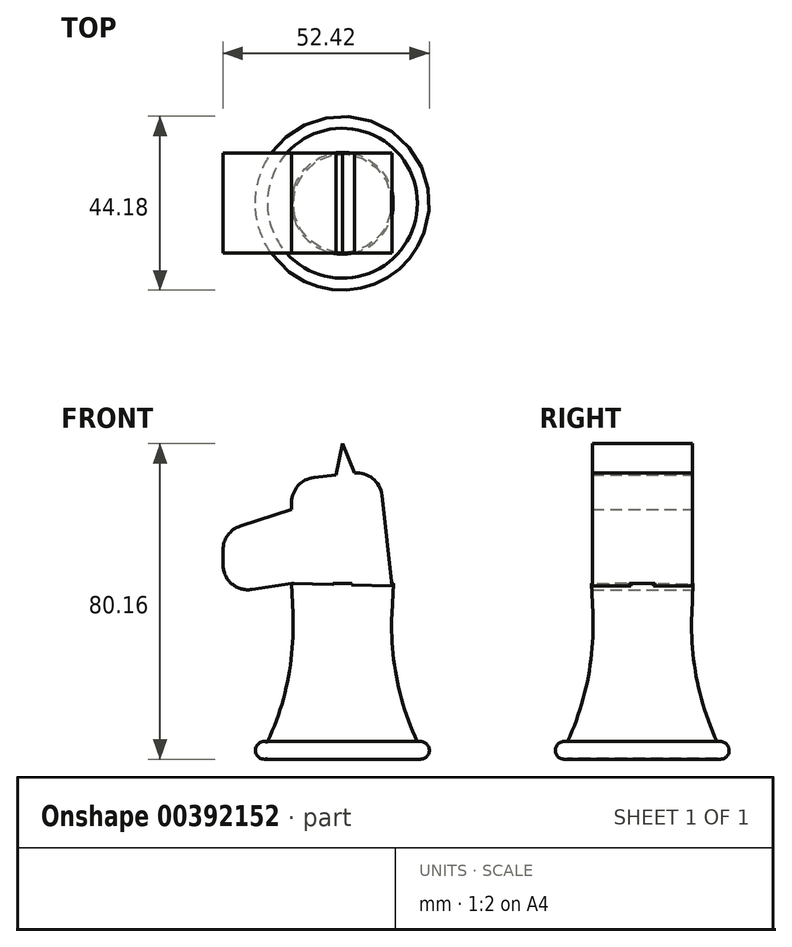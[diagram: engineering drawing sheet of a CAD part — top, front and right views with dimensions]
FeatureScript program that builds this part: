
annotation { "Feature Type Name" : "Feature", "Feature Type Description" : "" }
export const myFeature = defineFeature(function(context is Context, id is Id, definition is map)
    precondition{}
    {
        {
            var Q0;
            Q0=qCreatedBy(makeId("Front.planeOp"),FACE);
            var sketch = newSketch(context, id + "F0", { "sketchPlane" : qUnion([Q0])});
            skLineSegment(sketch, "E0", {"start": v(0, -50.97) * mm, "end": v(0, 6.18) * mm});
            skLineSegment(sketch, "E1", {"start": v(0, -50.97) * mm, "end": v(-19.05, -50.97) * mm});
            skArc(sketch, "E2", {"start": v(-19.05, -46.78) * mm, "mid": v(-22.09, -48.88) * mm, "end": v(-19.05, -50.97) * mm});
            skArc(sketch, "E3", {"start": v(-19.05, -46.78) * mm, "mid": v(-13.85, -30.88) * mm, "end": v(-12.58, -14.2) * mm});
            skLineSegment(sketch, "E4", {"start": v(-12.58, -14.2) * mm, "end": v(-12.92, -6.47) * mm});
            skLineSegment(sketch, "E5", {"start": v(-12.92, -6.47) * mm, "end": v(0, -6.47) * mm});
            skSolve(sketch);
        }
        {
            var Q0;
            Q0 = qSketchRegion(id + "F0", true);
            var Q1;
            Q1=sQuery(id+"F0.wireOp",EDGE,"E0");
            revolve(context, id + "F1", {"entities" : qUnion([Q0]), "axis" : qUnion([Q1]), "revolveType" : RevolveType.FULL});
        }
        {
            var Q0;
            Q0=qCreatedBy(makeId("Front.planeOp"),FACE);
            var sketch = newSketch(context, id + "F2", { "sketchPlane" : qUnion([Q0])});
            skLineSegment(sketch, "E6", {"start": v(12.58, -7.1) * mm, "end": v(10.05, 15.95) * mm});
            skLineSegment(sketch, "E7", {"start": v(3.04, 21.57) * mm, "end": v(-7.23, 20.44) * mm});
            skLineSegment(sketch, "E8", {"start": v(-12.88, 14.13) * mm, "end": v(-12.88, -6.45) * mm});
            skLineSegment(sketch, "E9", {"start": v(-12.88, -6.45) * mm, "end": v(12.58, -7.1) * mm});
            skLineSegment(sketch, "E10", {"start": v(-12.88, 12.3) * mm, "end": v(-25.93, 8.1) * mm});
            skPoint(sketch, "E10.endSnap0", {"position": v(-12.88, 6.68) * mm});
            skLineSegment(sketch, "E11", {"start": v(-12.88, -6.45) * mm, "end": v(-23.01, -8) * mm});
            skLineSegment(sketch, "E12", {"start": v(-30.33, -1.73) * mm, "end": v(-30.33, 2.06) * mm});
            skPoint(sketch, "E13.visualSharp", {"position": v(9.36, 22.26) * mm});
            skArc(sketch, "E13.filletArc", {"start": v(10.05, 15.95) * mm, "mid": v(7.71, 20.2) * mm, "end": v(3.04, 21.57) * mm});
            skPoint(sketch, "E14.visualSharp", {"position": v(-12.88, 19.82) * mm});
            skArc(sketch, "E14.filletArc", {"start": v(-7.23, 20.44) * mm, "mid": v(-11.26, 18.36) * mm, "end": v(-12.88, 14.13) * mm});
            skPoint(sketch, "E15.visualSharp", {"position": v(-30.33, 6.68) * mm});
            skArc(sketch, "E15.filletArc", {"start": v(-25.93, 8.1) * mm, "mid": v(-29.1, 5.8) * mm, "end": v(-30.33, 2.06) * mm});
            skPoint(sketch, "E16.visualSharp", {"position": v(-30.33, -9.13) * mm});
            skArc(sketch, "E16.filletArc", {"start": v(-30.33, -1.73) * mm, "mid": v(-28.11, -6.55) * mm, "end": v(-23.01, -8) * mm});
            skLineSegment(sketch, "E17", {"start": v(3.04, 21.57) * mm, "end": v(0, 29.04) * mm});
            skLineSegment(sketch, "E18", {"start": v(0, 29.04) * mm, "end": v(-1.58, 21.06) * mm});
            skSolve(sketch);
        }
        {
            var Q0;
            Q0 = qSketchRegion(id + "F2", true);
            extrude(context, id + "F3", {"entities" : qUnion([Q0]), "operationType" : NewBodyOperationType.ADD, "depth" : 12.7 * mm});
        }
        {
            var Q0;
            Q0 = qSketchRegion(id + "F2", true);
            extrude(context, id + "F4", {"entities" : qUnion([Q0]), "operationType" : NewBodyOperationType.ADD, "oppositeDirection" : true, "depth" : 12.7 * mm});
        }
    });
